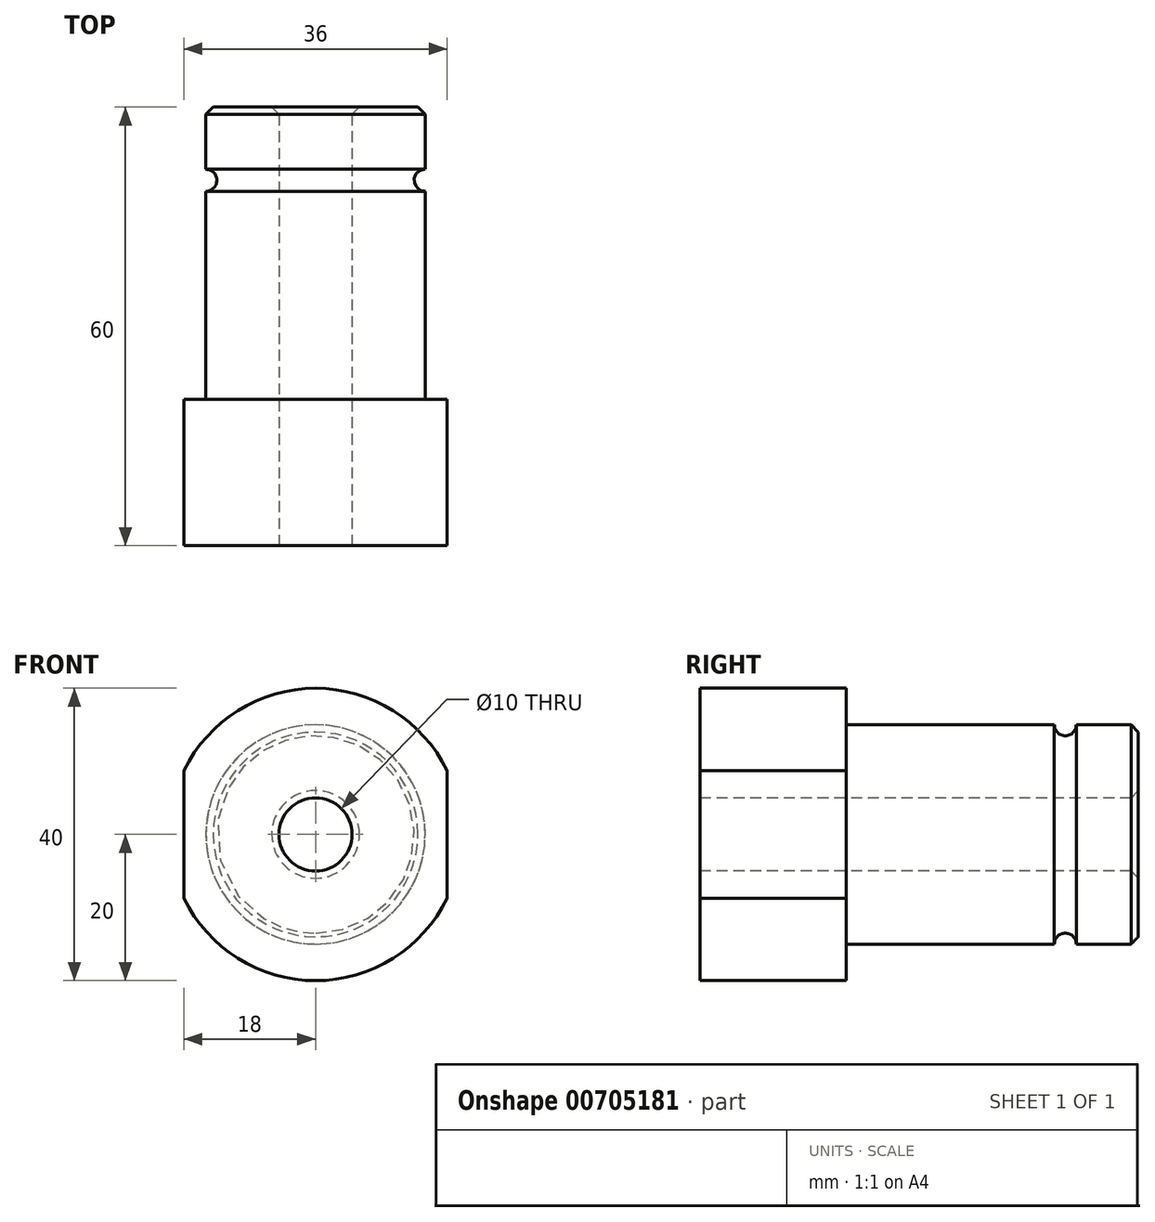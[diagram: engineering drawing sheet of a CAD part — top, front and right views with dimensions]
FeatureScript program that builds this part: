
annotation { "Feature Type Name" : "Feature", "Feature Type Description" : "" }
export const myFeature = defineFeature(function(context is Context, id is Id, definition is map)
    precondition{}
    {
        {
            var Q0;
            Q0=qCreatedBy(makeId("Front.planeOp"),FACE);
            var sketch = newSketch(context, id + "F0", { "sketchPlane" : qUnion([Q0])});
            skCircle(sketch, "E0", {"center": v(0, 0) * mm, "radius": 20 * mm});
            skSolve(sketch);
        }
        {
            var Q0;
            Q0=makeQuery(id+"F0.imprint","IMPRINT",FACE,{"disambiguationData":[TD([[makeQuery(id+"F0.imprint","IMPRINT",EDGE,{"derivedFrom":sQuery(id+"F0.wireOp",EDGE,"E0")}),1.0]])]});
            extrude(context, id + "F1", {"entities" : qUnion([Q0]), "oppositeDirection" : true, "depth" : 60 * mm, "offsetDistance" : 25 * mm});
        }
        {
            var Q0;
            Q0=makeQuery(id+"F1.opExtrude","CAP_FACE",FACE,{"disambiguationData":[OSD([sQuery(id+"F0.wireOp",EDGE,"E0")])],"isStart":true});
            var sketch = newSketch(context, id + "F2", { "sketchPlane" : qUnion([Q0])});
            skCircle(sketch, "E1", {"center": v(0, 0) * mm, "radius": 5 * mm});
            skSolve(sketch);
        }
        {
            var Q0;
            Q0=makeQuery(id+"F2.imprint","IMPRINT",FACE,{"disambiguationData":[TD([[makeQuery(id+"F2.imprint","IMPRINT",EDGE,{"derivedFrom":sQuery(id+"F2.wireOp",EDGE,"E1")}),1.0]])]});
            extrude(context, id + "F3", {"entities" : qUnion([Q0]), "operationType" : NewBodyOperationType.REMOVE, "endBound" : BoundingType.THROUGH_ALL, "oppositeDirection" : true, "depth" : 25 * mm, "offsetDistance" : 25 * mm});
        }
        {
            var Q0;
            Q0=makeQuery(id+"F1.opExtrude","CAP_FACE",FACE,{"disambiguationData":[OSD([sQuery(id+"F0.wireOp",EDGE,"E0")])],"isStart":true});
            var sketch = newSketch(context, id + "F4", { "sketchPlane" : qUnion([Q0])});
            skCircle(sketch, "E2", {"center": v(0, 0) * mm, "radius": 15 * mm});
            skSolve(sketch);
        }
        {
            var Q0;
            Q0=makeQuery(id+"F4.imprint","IMPRINT",FACE,{"disambiguationData":[TD([[makeQuery(id+"F4.imprint","IMPRINT",EDGE,{"derivedFrom":sQuery(id+"F4.wireOp",EDGE,"E2")}),-1.0]])]});
            extrude(context, id + "F5", {"entities" : qUnion([Q0]), "operationType" : NewBodyOperationType.REMOVE, "endBound" : BoundingType.THROUGH_ALL, "oppositeDirection" : true, "depth" : 40 * mm, "offsetDistance" : 25 * mm, "hasSecondDirection" : true, "secondDirectionOppositeDirection" : true, "secondDirectionDepth" : 20 * mm});
        }
        {
            var Q0;
            Q0=makeQuery(id+"F1.opExtrude","CAP_FACE",FACE,{"disambiguationData":[OSD([sQuery(id+"F0.wireOp",EDGE,"E0")])],"isStart":true});
            var sketch = newSketch(context, id + "F6", { "sketchPlane" : qUnion([Q0])});
            skArc(sketch, "E3", {"start": v(-18, -8.72) * mm, "mid": v(0, -20) * mm, "end": v(18, -8.72) * mm});
            skLineSegment(sketch, "E4", {"start": v(-18, 8.72) * mm, "end": v(-18, -8.72) * mm});
            skLineSegment(sketch, "E5", {"start": v(18, 8.72) * mm, "end": v(18, -8.72) * mm});
            skArc(sketch, "E6.trimOffspring", {"start": v(18, 8.72) * mm, "mid": v(0, 20) * mm, "end": v(-18, 8.72) * mm});
            skSolve(sketch);
        }
        {
            var Q0;
            Q0=makeQuery(id+"F6.imprint","IMPRINT",FACE,{"disambiguationData":[TD([[makeQuery(id+"F6.imprint","IMPRINT",EDGE,{"derivedFrom":sQuery(id+"F6.wireOp",EDGE,"E3")}),1.0]])]});
            extrude(context, id + "F7", {"entities" : qUnion([Q0]), "operationType" : NewBodyOperationType.INTERSECT, "endBound" : BoundingType.THROUGH_ALL, "depth" : 20 * mm, "offsetDistance" : 25 * mm, "hasSecondDirection" : true, "secondDirectionOppositeDirection" : true, "secondDirectionDepth" : 60 * mm});
        }
        {
            var Q0;
            Q0=qCreatedBy(makeId("Right.planeOp"),FACE);
            var sketch = newSketch(context, id + "F8", { "sketchPlane" : qUnion([Q0])});
            skLineSegment(sketch, "E7", {"start": v(0, 0) * mm, "end": v(77.88, 0) * mm, "construction": true});
            skLineSegment(sketch, "E8", {"start": v(-22.75, 15) * mm, "end": v(95.28, 15) * mm, "construction": true});
            skLineSegment(sketch, "E9", {"start": v(50, 49.37) * mm, "end": v(50, -28.62) * mm, "construction": true});
            skCircle(sketch, "E10", {"center": v(50, 15) * mm, "radius": 1.5 * mm});
            skSolve(sketch);
        }
        {
            var Q0;
            Q0=makeQuery(id+"F8.imprint","IMPRINT",FACE,{"disambiguationData":[TD([[makeQuery(id+"F8.imprint","IMPRINT",EDGE,{"derivedFrom":sQuery(id+"F8.wireOp",EDGE,"E10")}),1.0]])]});
            var Q1;
            Q1=sQuery(id+"F8.wireOp",EDGE,"E7");
            revolve(context, id + "F9", {"operationType" : NewBodyOperationType.REMOVE, "surfaceOperationType" : NewSurfaceOperationType.NEW, "entities" : qUnion([Q0]), "axis" : qUnion([Q1]), "revolveType" : RevolveType.FULL, "oppositeDirection" : true});
        }
        {
            var Q0;
            Q0=makeQuery(id+"F1.opExtrude","CAP_FACE",FACE,{"disambiguationData":[OSD([sQuery(id+"F0.wireOp",EDGE,"E0")])],"isStart":false});
            chamfer(context, id + "F10", {"entities" : qUnion([Q0]), "width" : 1 * mm, "tangentPropagation" : true});
        }
    });
